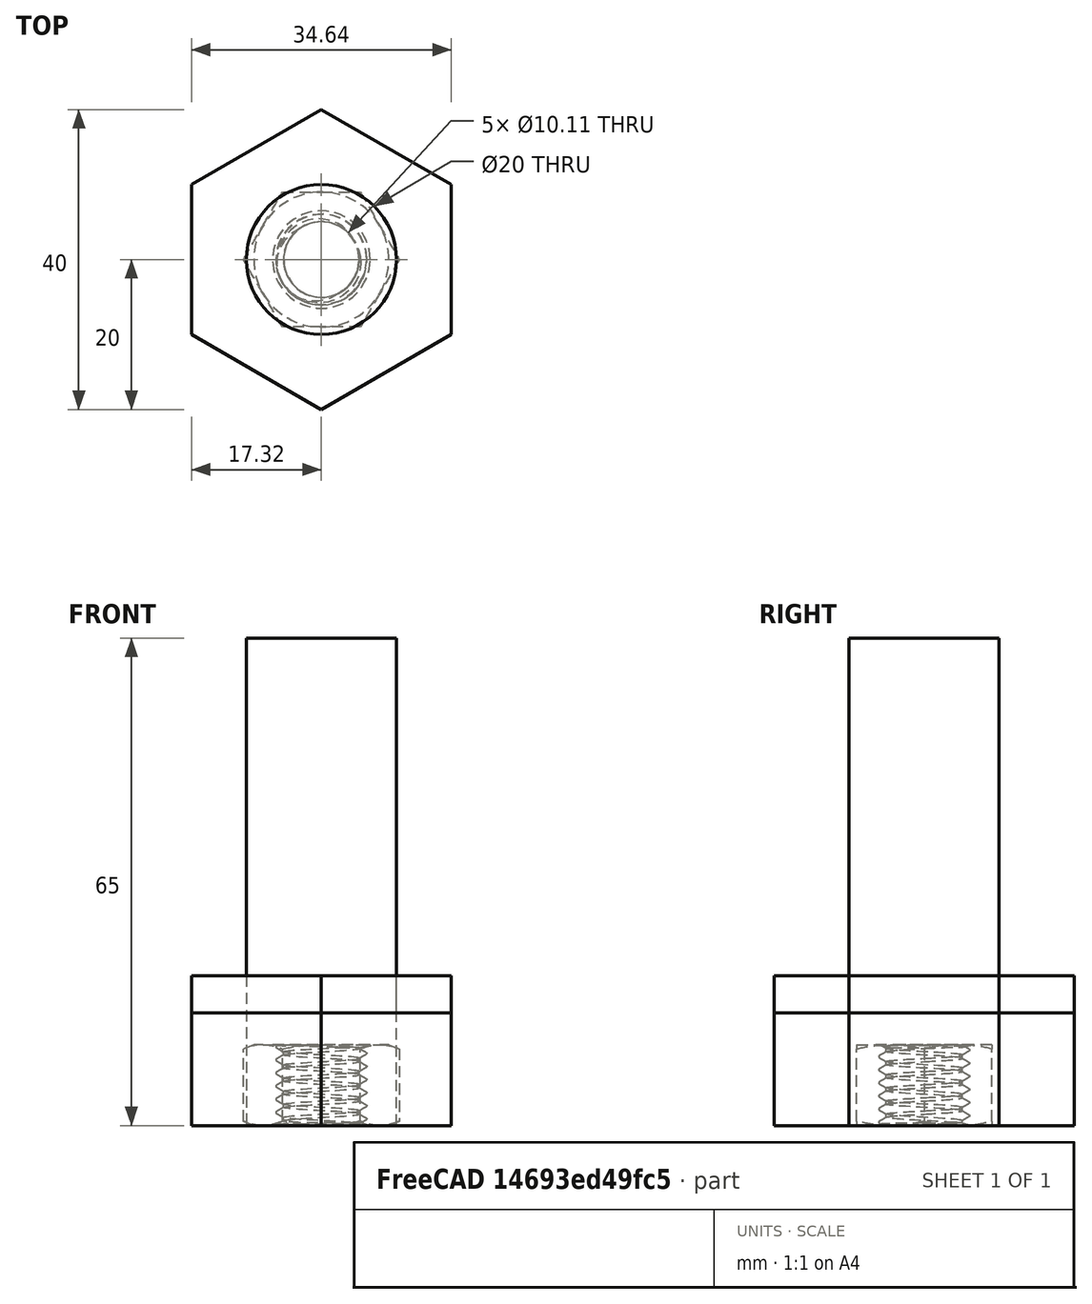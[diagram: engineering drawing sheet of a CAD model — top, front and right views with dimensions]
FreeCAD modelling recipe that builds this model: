
FCSTD DOCUMENT  (FreeCAD 1.0R39109 (Git))
Label: Unnamed
License: All rights reserved
LicenseURL: https://en.wikipedia.org/wiki/All_rights_reserved
objects: Sketcher::SketchObject×4, App::FeaturePython×4, PartDesign::Pad×3, PartDesign::Body×3, App::Link×3, Assembly::JointGroup×1, Assembly::AssemblyObject×1, Part::FeaturePython×1
note: 21 computed .brp shape members not serialized (recipe doc carries the construction recipe); baked Part::Feature solids carry a one-line shape summary decoded from their .brp

FEATURE [Sketcher::SketchObject] Sketch
  ArcFitTolerance = 1e-06
  AttachmentSupport = -> [XY_Plane]
  FullyConstrained = true
  MakeInternals = false
  MapMode = 5
  sketch-geometry (8):
    g0: LineSegment StartX=0 StartY=20 StartZ=0 EndX=-17.3205 EndY=10 EndZ=0
    g1: LineSegment StartX=-17.3205 StartY=10 StartZ=0 EndX=-17.3205 EndY=-10 EndZ=0
    g2: LineSegment StartX=-17.3205 StartY=-10 StartZ=0 EndX=-3.6e-15 EndY=-20 EndZ=0
    g3: LineSegment StartX=-3.6e-15 StartY=-20 StartZ=0 EndX=17.3205 EndY=-10 EndZ=0
    g4: LineSegment StartX=17.3205 StartY=-10 StartZ=0 EndX=17.3205 EndY=10 EndZ=0
    g5: LineSegment StartX=17.3205 StartY=10 StartZ=0 EndX=0 EndY=20 EndZ=0
    g6: Circle [constr] CenterX=0 CenterY=0 CenterZ=0 NormalX=0 NormalY=0 NormalZ=1 AngleXU=0 Radius=20
    g7: Circle CenterX=0 CenterY=0 CenterZ=0 NormalX=0 NormalY=0 NormalZ=1 AngleXU=0 Radius=10
  constraints (18):
    c: Coincident(g0,g1)
    c: Coincident(g1,g2)
    c: Coincident(g2,g3)
    c: Coincident(g3,g4)
    c: Coincident(g4,g5)
    c: Coincident(g5,g0)
    c: Equal(g0, g1-g5) x5
    c: PointOnObject(g0,g6)
    c: PointOnObject(g1,g6)
    c: PointOnObject(g2,g6)
    c: PointOnObject(g3,g6)
    c: PointOnObject(g4,g6)
    c: PointOnObject(g5,g6)
    c: Coincident(g6,g-1)
    c: PointOnObject(g5,g-2)
    c: Diameter(g7) = 20
    c: Coincident(g7,g6)
    c: DistanceY(g2,g0) = 40
FEATURE [PartDesign::Pad] Pad
  Direction = (0,0,1)
  Length = 20
  Length2 = 10
  Profile = -> Sketch
  ReferenceAxis = -> Sketch [N_Axis]
  Refine = true
  Suppressed = false
  Type = 0
FEATURE [PartDesign::Body] Body  label="NutBody"
  AllowCompound = false
  Group = -> [Sketch,Pad]
  Origin = -> Origin
  Tip = -> Pad
FEATURE [Sketcher::SketchObject] Sketch003
  ArcFitTolerance = 1e-06
  AttachmentSupport = -> [XZ_Plane002]
  FullyConstrained = false
  MakeInternals = false
  MapMode = 5
  Placement = pos=(0,0,0) rot=(1,0,0;1.5708rad)
  sketch-geometry (1):
    g0: LineSegment StartX=0 StartY=24.5435 StartZ=0 EndX=0 EndY=-15.2601 EndZ=0
  constraints (2):
    c: PointOnObject(g0,g-2)
    c: Vertical(g0)
FEATURE [PartDesign::Body] Body002  label="Helper"
  AllowCompound = false
  Group = -> [Sketch003]
  Origin = -> Origin002
FEATURE [Sketcher::SketchObject] Sketch004
  ArcFitTolerance = 1e-06
  AttachmentSupport = -> [XY_Plane001]
  FullyConstrained = true
  MakeInternals = false
  MapMode = 5
  sketch-geometry (7):
    g0: LineSegment StartX=0 StartY=20 StartZ=0 EndX=-17.3205 EndY=10 EndZ=0
    g1: LineSegment StartX=-17.3205 StartY=10 StartZ=0 EndX=-17.3205 EndY=-10 EndZ=0
    g2: LineSegment StartX=-17.3205 StartY=-10 StartZ=0 EndX=0 EndY=-20 EndZ=0
    g3: LineSegment StartX=0 StartY=-20 StartZ=0 EndX=17.3205 EndY=-10 EndZ=0
    g4: LineSegment StartX=17.3205 StartY=-10 StartZ=0 EndX=17.3205 EndY=10 EndZ=0
    g5: LineSegment StartX=17.3205 StartY=10 StartZ=0 EndX=0 EndY=20 EndZ=0
    g6: Circle [constr] CenterX=0 CenterY=0 CenterZ=0 NormalX=0 NormalY=0 NormalZ=1 AngleXU=0 Radius=20
  constraints (16):
    c: Coincident(g0,g1)
    c: Coincident(g1,g2)
    c: Coincident(g2,g3)
    c: Coincident(g3,g4)
    c: Coincident(g4,g5)
    c: Coincident(g5,g0)
    c: Equal(g0, g1-g5) x5
    c: PointOnObject(g0,g6)
    c: PointOnObject(g1,g6)
    c: PointOnObject(g2,g6)
    c: PointOnObject(g3,g6)
    c: PointOnObject(g4,g6)
    c: PointOnObject(g5,g6)
    c: Coincident(g6,g-1)
    c: PointOnObject(g5,g-2)
    c: Distance(g0,g3) = 40
FEATURE [PartDesign::Pad] Pad001
  Direction = (0,0,1)
  Length = 15
  Length2 = 10
  Profile = -> Sketch004
  ReferenceAxis = -> Sketch004 [N_Axis]
  Refine = true
  Suppressed = false
  Type = 0
FEATURE [Sketcher::SketchObject] Sketch005
  ArcFitTolerance = 1e-06
  AttachmentSupport = -> [Pad001]
  FullyConstrained = true
  MakeInternals = false
  MapMode = 5
  Placement = pos=(0,0,15) rot=(0,0,1;0rad)
  sketch-geometry (1):
    g0: Circle CenterX=0 CenterY=0 CenterZ=0 NormalX=0 NormalY=0 NormalZ=1 AngleXU=0 Radius=10
  constraints (2):
    c: Diameter(g0) = 20
    c: Coincident(g0,g-1)
FEATURE [PartDesign::Pad] Pad002
  BaseFeature = -> Pad001
  Direction = (0,0,1)
  Length = 50
  Length2 = 10
  Profile = -> Sketch005 [Edge1]
  ReferenceAxis = -> Sketch005 [N_Axis]
  Refine = true
  Suppressed = false
  Type = 0
FEATURE [PartDesign::Body] Body001  label="BoltBody"
  AllowCompound = false
  Group = -> [Sketch004,Pad001,Sketch005,Pad002]
  Origin = -> Origin001
  Tip = -> Pad002
FEATURE [App::Link] NutBody  label="NutBody001"
  LinkPlacement = pos=(144.105,14.019,26.7022) rot=(0.862171,-0.452351,-0.228122;1.39454rad)
  LinkedObject = -> Body
  Placement = pos=(144.105,14.019,26.7022) rot=(0.862171,-0.452351,-0.228122;1.39454rad)
FEATURE [App::Link] BoltBody  label="BoltBody001"
  LinkPlacement = pos=(169.55,46.0051,17.5612) rot=(0.810631,-0.047449,-0.583632;1.75747rad)
  LinkedObject = -> Body001
  Placement = pos=(169.55,46.0051,17.5612) rot=(0.810631,-0.047449,-0.583632;1.75747rad)
FEATURE [App::Link] Helper  label="Helper001"
  LinkPlacement = pos=(134.774,2.28962,30.0542) rot=(-0.471377,-0.419246,0.77591;3.40935rad)
  LinkedObject = -> Body002
  Placement = pos=(134.774,2.28962,30.0542) rot=(-0.471377,-0.419246,0.77591;3.40935rad)
FEATURE [App::FeaturePython] Joint002  label="Screw"  # Assembly joint (typed FeaturePython)
  Activated = true
  AngleMax = 0
  AngleMin = 0
  Detach1 = false
  Detach2 = false
  Distance = 20
  Distance2 = 0
  EnableAngleMax = false
  EnableAngleMin = false
  EnableLengthMax = false
  EnableLengthMin = false
  JointType = 10 (Screw)
  LengthMax = 0
  LengthMin = 0
  Placement1 = pos=(17.3205,10,7.5) rot=(0,0,1;0rad)
  Placement2 = pos=(17.3205,-10,10) rot=(0,0,1;0rad)
  Reference1 = -> Assembly [BoltBody.Edge5,BoltBody.Edge5]
  Reference2 = -> Assembly [NutBody.Edge11,NutBody.Edge11]
FEATURE [App::FeaturePython] GroundedJoint  # Assembly grounded joint (typed FeaturePython)
  ObjectToGround = -> BoltBody
  Placement = pos=(169.55,46.0051,17.5612) rot=(0.810631,-0.047449,-0.583632;1.75747rad)
FEATURE [App::FeaturePython] Joint  label="Slider"  # Assembly joint (typed FeaturePython)
  Activated = true
  AngleMax = 0
  AngleMin = 0
  Detach1 = false
  Detach2 = false
  Distance = 0
  Distance2 = 0
  EnableAngleMax = false
  EnableAngleMin = false
  EnableLengthMax = true
  EnableLengthMin = true
  JointType = 3 (Slider)
  LengthMax = 0.55
  LengthMin = -29.45
  Placement1 = pos=(0,4.64166,0) rot=(-0.57735,-0.57735,0.57735;4.18879rad)
  Placement2 = pos=(7.1e-15,-1.42e-14,65) rot=(0,0,1;0rad)
  Reference1 = -> Assembly [Helper.Sketch003.Edge1,Helper.Sketch003.Edge1]
  Reference2 = -> Assembly [BoltBody.Edge21,BoltBody.Edge21]
FEATURE [App::FeaturePython] Joint003  label="Revolute"  # Assembly joint (typed FeaturePython)
  Activated = true
  AngleMax = 0
  AngleMin = 0
  Detach1 = false
  Detach2 = false
  Distance = 0
  Distance2 = 0
  EnableAngleMax = false
  EnableAngleMin = false
  EnableLengthMax = false
  EnableLengthMin = false
  JointType = 1 (Revolute)
  LengthMax = 0
  LengthMin = 0
  Placement1 = pos=(0,4.64166,0) rot=(-0.57735,-0.57735,0.57735;4.18879rad)
  Placement2 = pos=(0,0,20) rot=(0,0,1;0rad)
  Reference1 = -> Assembly [Helper.Sketch003.Edge1,Helper.Sketch003.Edge1]
  Reference2 = -> Assembly [NutBody.Edge21,NutBody.Edge21]
FEATURE [Assembly::JointGroup] Joints
  Group = -> [Joint002,GroundedJoint,Joint,Joint003]
FEATURE [Assembly::AssemblyObject] Assembly
  Group = -> [Joints,NutBody,BoltBody,Helper,Joint002,GroundedJoint,Joint,Joint003]
  Origin = -> Origin003
  Type = Assembly
FEATURE [Part::FeaturePython] Nut  label="M12-Nut"  # WARN: FeaturePython — macro-defined, semantics opaque (R4)
  Diameter = 11
  Invert = false
  LeftHanded = false
  MatchOuter = false
  OffsetAngle = 0
  Thread = true
  Type = 31
